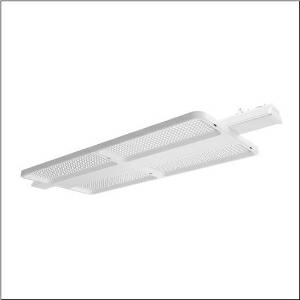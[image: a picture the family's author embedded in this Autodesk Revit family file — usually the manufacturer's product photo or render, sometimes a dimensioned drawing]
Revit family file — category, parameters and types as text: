
# Revit family: highbay_21_fur_licross_r__tragschiene_maxi_52hn11db6lla_ad8f
name_source: partatom
category: Lighting Fixtures
units: mm (PartAtom-declared; Revit-internal decimal feet)

## family parameters
Cut with Voids When Loaded = No
Host = Face
Light Source = No
Part Type = Normal
Room Calculation Point = No
Round Connector Dimension = Use Diameter
Shared = No

## types (1)
- --- (1 x LED, 4100 lm, 22.6 W, 6500K)
    Apparent Load = 23 VA
    CIE Flux Codes = 89 97 99 100 100
    Color Rendering = 80
    Color Temperature = 6500K
    Default Elevation = 1800 mm
    Description = high bay luminaire Highbay 21 for Licross® trunking rail maxi; direct symmetric narrow distribution, light control with lens of PMMA; UGR ≤ 19 (X = 4H | Y = 8H | S = 0.25H | reflection values 70/50/20); luminous flux: 27.140lm; light colour: 865, colour temperature: 6500K, MacAdam ≤ 3 SDCM (initial), colour rendering: CRI > 80; luminous efficacy: 188,5lm/W; rated service life: 75.000h (L80/B50) at AT= ta max; control: DALI 2; luminaire connection: plug, 5-pole, with phase selectionmains connection: 230..240V, AC 50/60Hz; connected load: 144W; protection rating (complete): IP64; insulation class (complete): insulation class I (protective earthing); protection symbol: D; impact resistance: IK07; certification: CE, ENEC, VDE, UKCA; internal wiring halogen-free; luminaire corresponds to IFS (International Featured Standards) requirements for safety and quality in the food industry; LABS conformity tested according to VDMA 24364:2018-05; housing frame of high-performance plastic PA6, matt traffic white (RAL 9016); cover of PMMA; fixing on rail side of steel, galvanised, white; blank cover of PC/ABS, traffic white (RAL 9016); dimension (LxWxH): 1.250 x 442 x 71mm; permissible operating ambient temperature: -40..+55°C (reducing of maximum allowable ambient temperature of 5°C with ceiling mounting); packaging unit: 1 piece
    Height = 72 mm  [stored 0.23622 ft]
    Lamp = 1 x LED
    Lamp Light Flux = 4100 lm
    Lamp Power = 22.6 W
    Lamp count = 1
    Length = 946 mm
    Luminous efficacy = 181 lm/W
    Manufacturer = Siteco
    ModVariant = No
    Model = 52HN11DB6LLA
    Mounting Place = Ceiling
    Mounting Type = Pendant
    Number of Poles = 1
    OnlyDefault = Yes
    Power Factor = 1
    Product Name = Highbay 21 für Licross® Tragschiene maxi
    Product group = high bay luminaire
    ProductGroupID = 901
    Protection Class = Protection class I
    Protection Degree = IP 64
    RLX_Detail_Level = 1
    RLX_Emergency_Light_Flux = 0 lm
    RLX_Emergency_Type = 0
    RLX_Emergency_Type_DB = No
    RlxData = <blob elided: 130305 chars, md5=80bf7046>
    Socket = socket
    Standby Power = 0 W
    System Light Flux = 4100 lm
    System Power = 23 W
    Type Comments = : DC mode (central or group accumulator) initial emergency light level
    Type Image = l_1361711.jpg
    URL = http://relux.com
    VarID = @adj_000987
    Voltage = 0 V
    Weight = 0.00 kg
    Width = 442 mm

note: [stored X ft] marks values corroborated as IEEE doubles in the binary element streams (Revit-internal decimal feet)

## geometry (parser evidence)
native form markers: Blend x4, Sweep x10
no freeform markers — native parametric forms only
